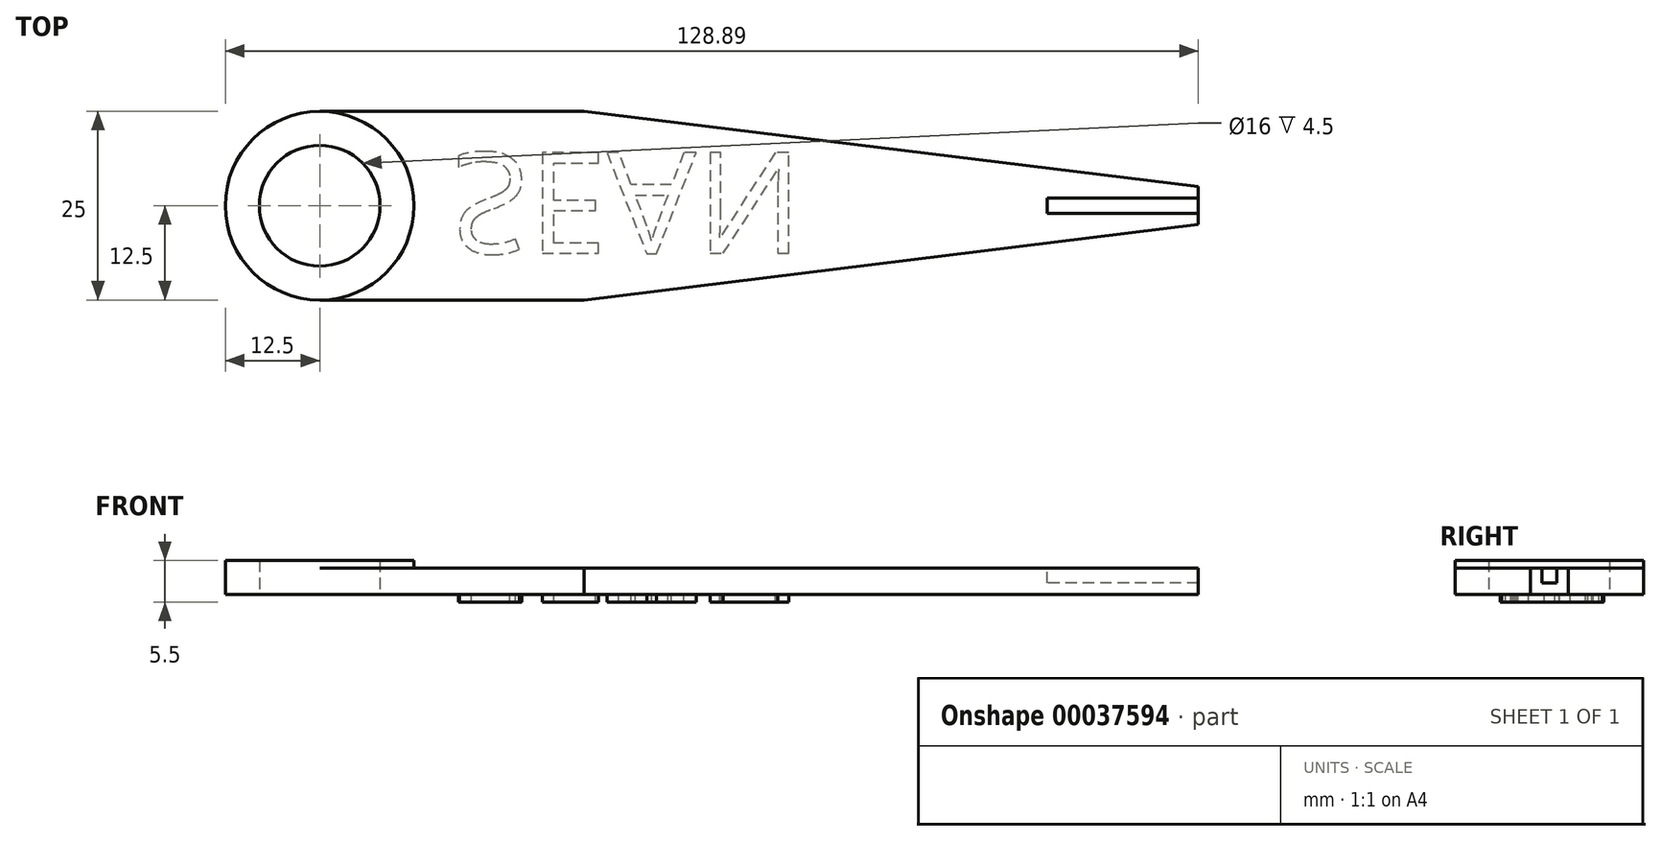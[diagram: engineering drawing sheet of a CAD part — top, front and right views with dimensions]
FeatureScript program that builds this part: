
annotation { "Feature Type Name" : "Feature", "Feature Type Description" : "" }
export const myFeature = defineFeature(function(context is Context, id is Id, definition is map)
    precondition{}
    {
        {
            var Q0;
            Q0=qCreatedBy(makeId("Top.planeOp"),FACE);
            var sketch = newSketch(context, id + "F0", { "sketchPlane" : qUnion([Q0])});
            skCircle(sketch, "E0", {"center": v(0, 0) * mm, "radius": 8 * mm});
            skCircle(sketch, "E1", {"center": v(0, 0) * mm, "radius": 12.5 * mm});
            skLineSegment(sketch, "E2", {"start": v(0, 12.5) * mm, "end": v(35, 12.5) * mm});
            skPoint(sketch, "E3", {"position": v(0, 12.5) * mm});
            skLineSegment(sketch, "E4", {"start": v(0, 0) * mm, "end": v(42.9, 0) * mm, "construction": true});
            skLineSegment(sketch, "E5.MirrorCS", {"start": v(0, -12.5) * mm, "end": v(35, -12.5) * mm});
            skLineSegment(sketch, "E6", {"start": v(35, 12.5) * mm, "end": v(96.2, 12.5) * mm, "construction": true});
            skPoint(sketch, "E7.orphan", {"position": v(35, -12.5) * mm});
            skPoint(sketch, "E8.MirrorCS.end.orphan", {"position": v(238.6, 12.5) * mm});
            skPoint(sketch, "E9.end.orphan", {"position": v(238.6, -12.5) * mm});
            skLineSegment(sketch, "E10", {"start": v(35, 12.5) * mm, "end": v(116.39, 2.5) * mm});
            skLineSegment(sketch, "E11.MirrorCS", {"start": v(35, -12.5) * mm, "end": v(116.39, -2.5) * mm});
            skLineSegment(sketch, "E12", {"start": v(116.39, 2.5) * mm, "end": v(116.39, -2.5) * mm});
            skSolve(sketch);
        }
        {
            var Q0;
            Q0 = qSketchRegion(id + "F0", true);
            extrude(context, id + "F1", {"entities" : qUnion([Q0]), "depth" : 3.5 * mm});
        }
        {
            var Q0;
            Q0=makeQuery(id+"F1.opExtrude","CAP_FACE",FACE,{"disambiguationData":[OSD([sQuery(id+"F0.wireOp",EDGE,"E0"),sQuery(id+"F0.wireOp",EDGE,"E1"),sQuery(id+"F0.wireOp",EDGE,"E2"),sQuery(id+"F0.wireOp",EDGE,"E5.MirrorCS"),sQuery(id+"F0.wireOp",EDGE,"E10"),sQuery(id+"F0.wireOp",EDGE,"E11.MirrorCS"),sQuery(id+"F0.wireOp",EDGE,"E12")])],"isStart":false});
            var sketch = newSketch(context, id + "F2", { "sketchPlane" : qUnion([Q0])});
            skCircle(sketch, "E13", {"center": v(0, 0) * mm, "radius": 12.5 * mm});
            skCircle(sketch, "E14", {"center": v(0, 0) * mm, "radius": 8 * mm});
            skSolve(sketch);
        }
        {
            var Q0;
            Q0=makeQuery(id+"F2.imprint","IMPRINT",FACE,{"disambiguationData":[TD([[makeQuery(id+"F2.imprint","IMPRINT",EDGE,{"derivedFrom":sQuery(id+"F2.wireOp",EDGE,"E14")}),-1.0]])]});
            extrude(context, id + "F3", {"entities" : qUnion([Q0]), "operationType" : NewBodyOperationType.ADD, "depth" : 1 * mm});
        }
        {
            var Q0;
            Q0=makeQuery(id+"F1.opExtrude","CAP_FACE",FACE,{"disambiguationData":[OSD([sQuery(id+"F0.wireOp",EDGE,"E0"),sQuery(id+"F0.wireOp",EDGE,"E1"),sQuery(id+"F0.wireOp",EDGE,"E2"),sQuery(id+"F0.wireOp",EDGE,"E5.MirrorCS"),sQuery(id+"F0.wireOp",EDGE,"E10"),sQuery(id+"F0.wireOp",EDGE,"E11.MirrorCS"),sQuery(id+"F0.wireOp",EDGE,"E12")])],"isStart":false});
            var sketch = newSketch(context, id + "F4", { "sketchPlane" : qUnion([Q0])});
            skLineSegment(sketch, "E15.bottom", {"start": v(116.39, 1) * mm, "end": v(96.39, 1) * mm});
            skLineSegment(sketch, "E15.top", {"start": v(116.39, -1) * mm, "end": v(96.39, -1) * mm});
            skLineSegment(sketch, "E15.left", {"start": v(116.39, 1) * mm, "end": v(116.39, -1) * mm});
            skLineSegment(sketch, "E15.right", {"start": v(96.39, 1) * mm, "end": v(96.39, -1) * mm});
            skSolve(sketch);
        }
        {
            var Q0;
            Q0=makeQuery(id+"F4.imprint","IMPRINT",FACE,{"disambiguationData":[TD([[makeQuery(id+"F4.imprint","IMPRINT",EDGE,{"derivedFrom":sQuery(id+"F4.wireOp",EDGE,"E15.bottom")}),1.0]])]});
            extrude(context, id + "F5", {"entities" : qUnion([Q0]), "operationType" : NewBodyOperationType.REMOVE, "oppositeDirection" : true, "depth" : 2 * mm});
        }
        {
            var Q0;
            Q0=makeQuery(id+"F1.opExtrude","CAP_FACE",FACE,{"disambiguationData":[OSD([sQuery(id+"F0.wireOp",EDGE,"E0"),sQuery(id+"F0.wireOp",EDGE,"E1"),sQuery(id+"F0.wireOp",EDGE,"E2"),sQuery(id+"F0.wireOp",EDGE,"E5.MirrorCS"),sQuery(id+"F0.wireOp",EDGE,"E10"),sQuery(id+"F0.wireOp",EDGE,"E11.MirrorCS"),sQuery(id+"F0.wireOp",EDGE,"E12")])],"isStart":true});
            var sketch = newSketch(context, id + "F6", { "sketchPlane" : qUnion([Q0])});
            skText(sketch, "E16", { "text": "SEAN", "fontName": "OpenSans-Regular.ttf"});
            const initialGuessF6  = {"E16": [0.0174, -0.00702, 1, 0, 0.01345]};
            skSetInitialGuess(sketch, initialGuessF6);
            skSolve(sketch);
        }
        {
            var Q0;
            Q0 = qSketchRegion(id + "F6", true);
            extrude(context, id + "F7", {"entities" : qUnion([Q0]), "operationType" : NewBodyOperationType.ADD, "depth" : 1 * mm});
        }
    });
